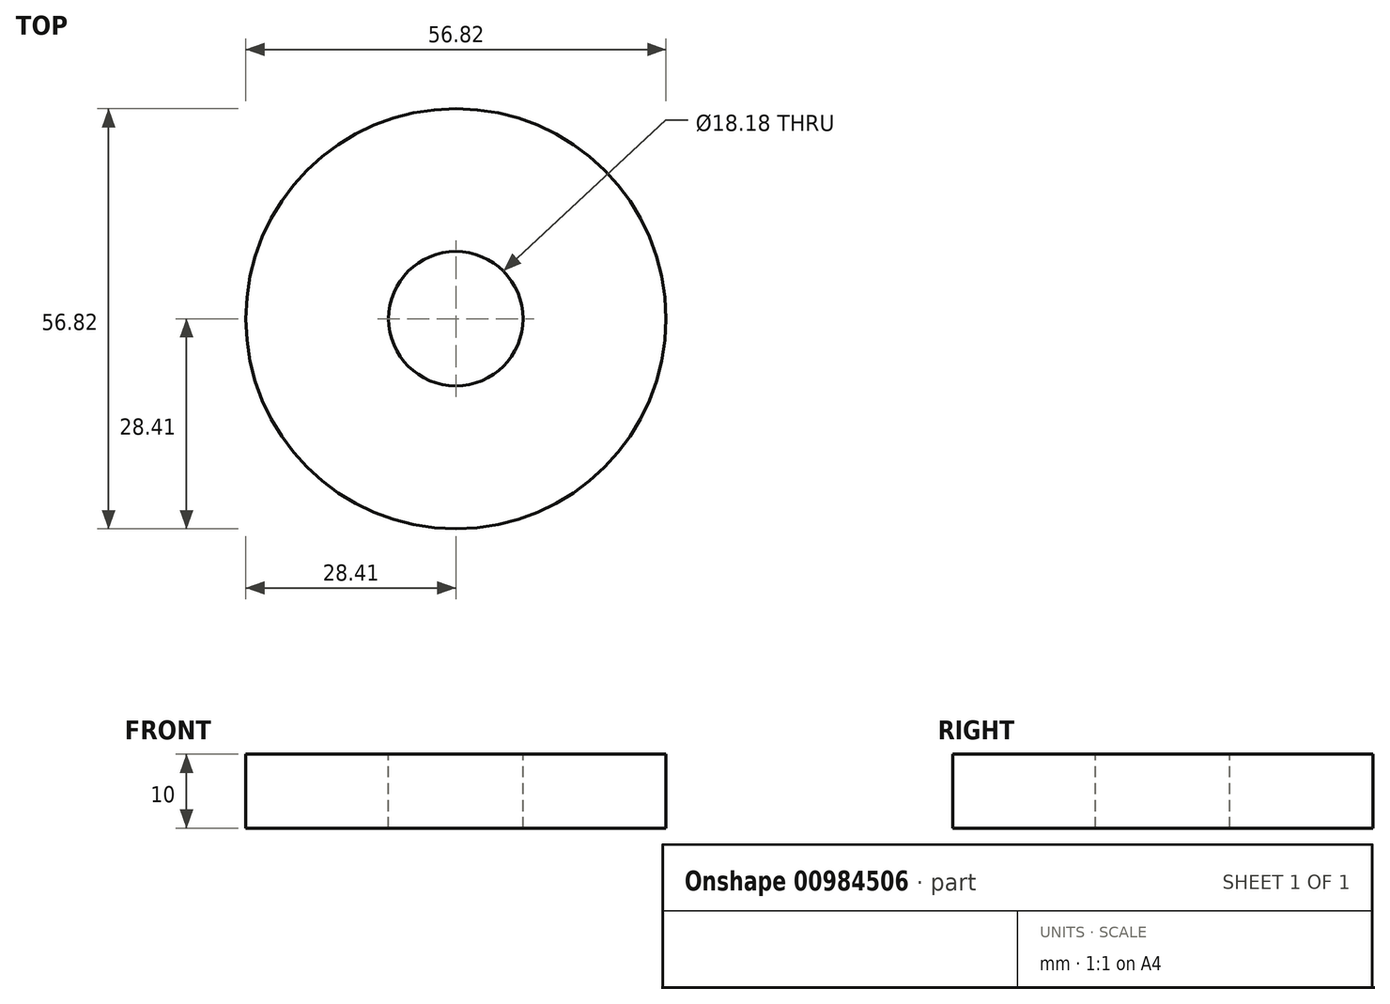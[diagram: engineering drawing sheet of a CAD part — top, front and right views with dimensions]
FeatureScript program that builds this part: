
annotation { "Feature Type Name" : "Feature", "Feature Type Description" : "" }
export const myFeature = defineFeature(function(context is Context, id is Id, definition is map)
    precondition{}
    {
        {
            var Q0;
            Q0=qCreatedBy(makeId("Top.planeOp"),FACE);
            var sketch = newSketch(context, id + "F0", { "sketchPlane" : qUnion([Q0])});
            skCircle(sketch, "E0", {"center": v(0, 0) * mm, "radius": 28.4 * mm});
            skSolve(sketch);
        }
        {
            var Q0;
            Q0 = qSketchRegion(id + "F0", false);
            extrude(context, id + "F1", {"entities" : qUnion([Q0]), "depth" : 10 * mm});
        }
        {
            var Q0;
            Q0=makeQuery(id+"F1.opExtrude","CAP_FACE",FACE,{"disambiguationData":[OSD([sQuery(id+"F0.wireOp",EDGE,"E0")])],"isStart":false});
            var sketch = newSketch(context, id + "F2", { "sketchPlane" : qUnion([Q0])});
            skCircle(sketch, "E1", {"center": v(0, 0) * mm, "radius": 9.1 * mm});
            skSolve(sketch);
        }
        {
            var Q0;
            Q0 = qSketchRegion(id + "F2", false);
            extrude(context, id + "F3", {"entities" : qUnion([Q0]), "operationType" : NewBodyOperationType.REMOVE, "depth" : 10 * mm, "oppositeDirection" : true});
        }
    });
